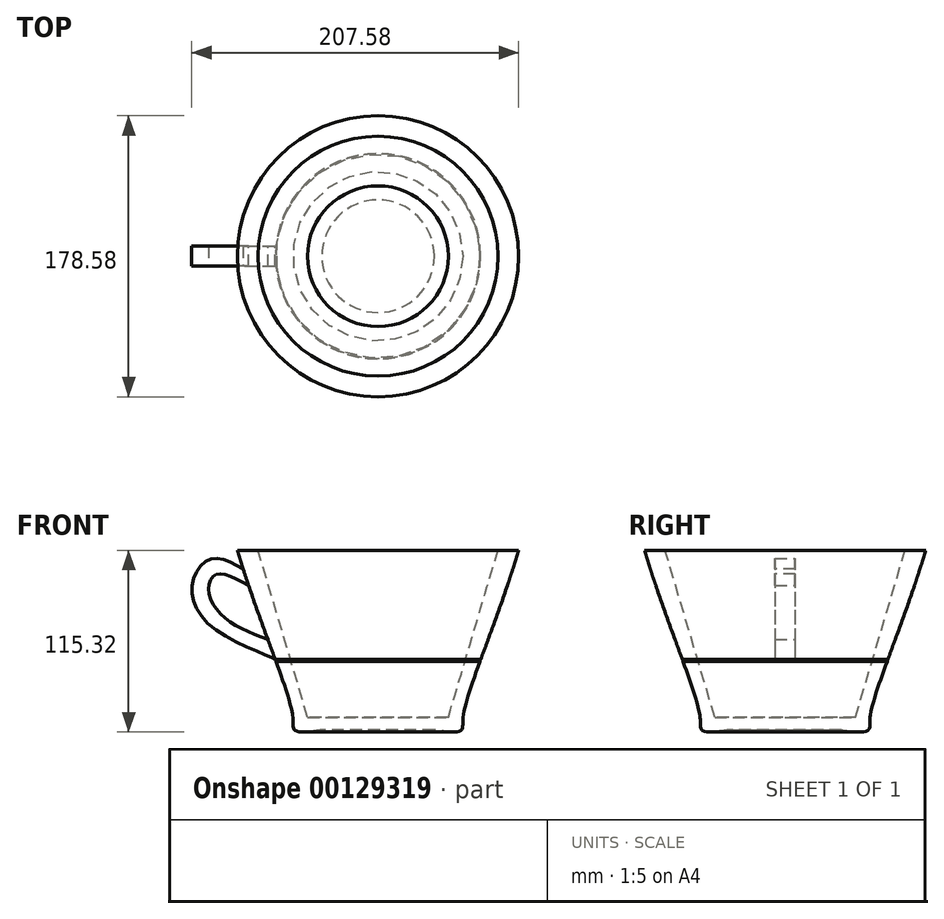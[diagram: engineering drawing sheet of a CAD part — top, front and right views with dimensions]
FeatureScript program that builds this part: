
annotation { "Feature Type Name" : "Feature", "Feature Type Description" : "" }
export const myFeature = defineFeature(function(context is Context, id is Id, definition is map)
    precondition{}
    {
        {
            var Q0;
            Q0=qCreatedBy(makeId("Front.planeOp"),FACE);
            var sketch = newSketch(context, id + "F0", { "sketchPlane" : qUnion([Q0])});
            skFitSpline(sketch, "E0", {"points": [v(-30.5, 42.82) * mm, v(4.91, -64.96) * mm, v(23.05, -71.26) * mm], "startDerivative": vector(63.52, -212.66) * mm, "endDerivative": vector(211.96, 30.77) * mm});
            skLineSegment(sketch, "E1", {"start": v(23.05, -71.26) * mm, "end": v(58.8, -71.26) * mm});
            skLineSegment(sketch, "E2", {"start": v(-30.5, 42.82) * mm, "end": v(-17.4, 42.82) * mm});
            skLineSegment(sketch, "E3", {"start": v(-17.4, 42.82) * mm, "end": v(14.11, -63.26) * mm});
            skLineSegment(sketch, "E4", {"start": v(14.11, -63.26) * mm, "end": v(58.8, -63.26) * mm});
            skLineSegment(sketch, "E5", {"start": v(58.8, -63.26) * mm, "end": v(58.8, -71.26) * mm});
            skFitSpline(sketch, "E6", {"points": [v(-26.78, 30.83) * mm, v(-47.04, 37.4) * mm, v(-59.26, 20.93) * mm, v(-44.21, -7.76) * mm, v(-6.42, -26.64) * mm, v(-6.06, -27.64) * mm], "startDerivative": vector(-104.47, 58.72) * mm, "endDerivative": vector(-2.87, -19.55) * mm});
            skFitSpline(sketch, "E7", {"points": [v(-23.39, 20.51) * mm, v(-43.74, 27.52) * mm, v(-48.92, 17.64) * mm, v(-38.57, 0) * mm, v(-11.15, -13.84) * mm], "startDerivative": vector(-92.98, 49.16) * mm, "endDerivative": vector(99.65, -36.9) * mm});
            skSolve(sketch);
        }
        {
            var Q0;
            {var subQ3=sQuery(id+"F0.wireOp",EDGE,"E7");Q0=makeQuery(id+"F0.imprint","IMPRINT",FACE,{"disambiguationData":[TD([[makeQuery(id+"F0.imprint","IMPRINT",EDGE,{"derivedFrom":subQ3}),-1.0]])]});}
            extrude(context, id + "F1", {"entities" : qUnion([Q0]), "endBound" : BoundingType.SYMMETRIC, "depth" : 12.7 * mm});
        }
        {
            var Q0;
            {var subQ4=sQuery(id+"F0.wireOp",EDGE,"E1");Q0=makeQuery(id+"F0.imprint","IMPRINT",FACE,{"disambiguationData":[TD([[makeQuery(id+"F0.imprint","IMPRINT",EDGE,{"derivedFrom":subQ4}),1.0]])]});}
            var Q1;
            Q1=sQuery(id+"F0.wireOp",EDGE,"E5");
            revolve(context, id + "F2", {"operationType" : NewBodyOperationType.ADD, "entities" : qUnion([Q0]), "axis" : qUnion([Q1]), "revolveType" : RevolveType.FULL});
        }
    });
